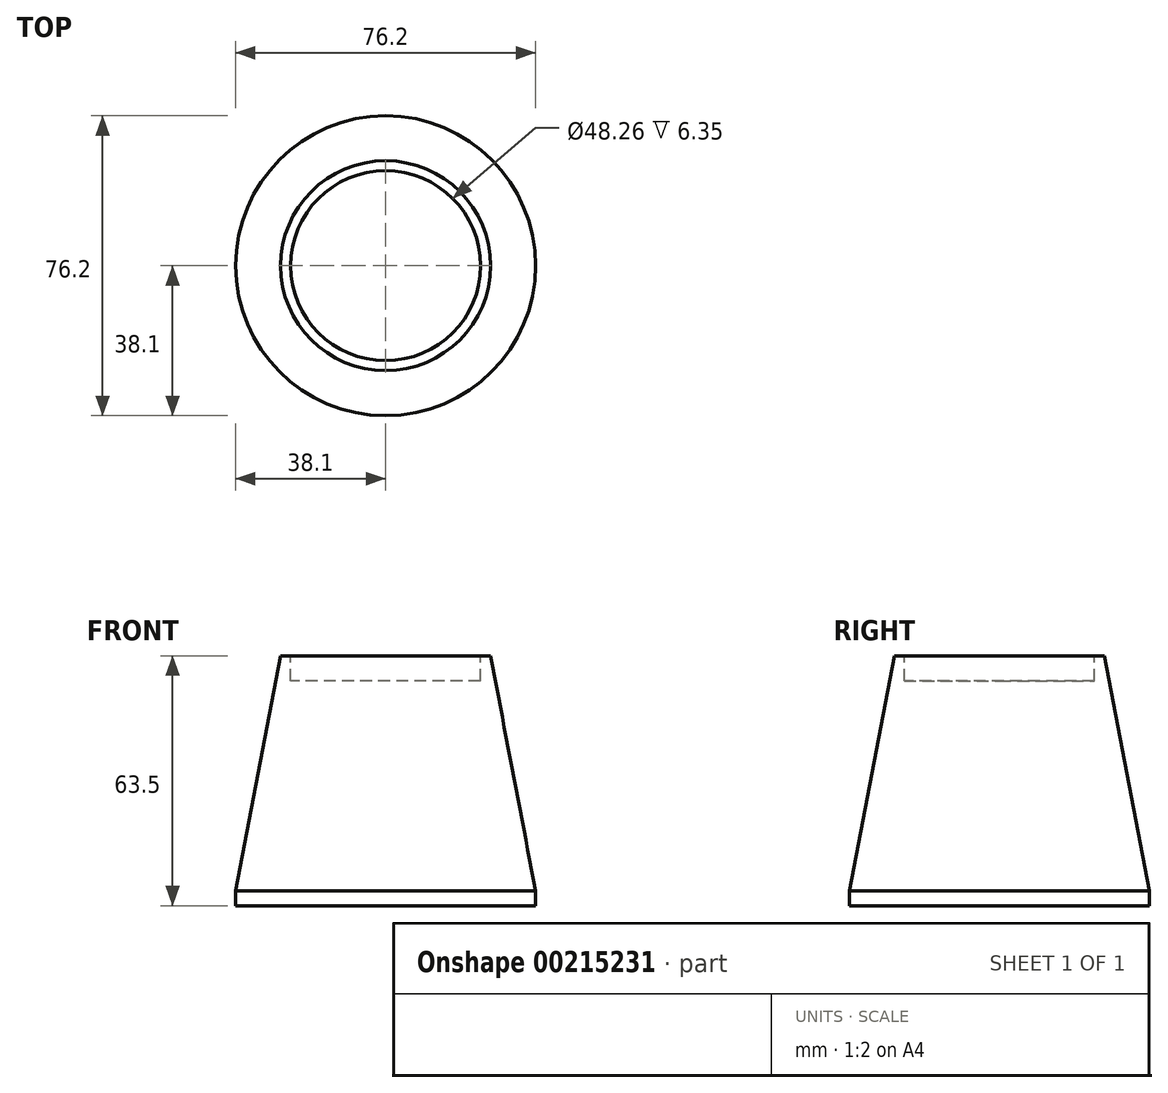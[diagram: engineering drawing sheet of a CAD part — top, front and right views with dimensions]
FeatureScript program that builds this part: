
annotation { "Feature Type Name" : "Feature", "Feature Type Description" : "" }
export const myFeature = defineFeature(function(context is Context, id is Id, definition is map)
    precondition{}
    {
        {
            var Q0;
            Q0=qCreatedBy(makeId("Top.planeOp"),FACE);
            var sketch = newSketch(context, id + "F0", { "sketchPlane" : qUnion([Q0])});
            skCircle(sketch, "E0", {"center": v(0, 0) * mm, "radius": 38.1 * mm});
            skSolve(sketch);
        }
        {
            var Q0;
            Q0=makeQuery(id+"F0.imprint","IMPRINT",FACE,{"disambiguationData":[TD([[makeQuery(id+"F0.imprint","IMPRINT",EDGE,{"derivedFrom":sQuery(id+"F0.wireOp",EDGE,"E0")}),1.0]])]});
            extrude(context, id + "F1", {"entities" : qUnion([Q0]), "depth" : 3.8 * mm});
        }
        {
            var Q0;
            Q0=qCreatedBy(makeId("Top.planeOp"),FACE);
            cPlane(context, id + "F2", {"entities" : qUnion([Q0]), "cplaneType" : CPlaneType.OFFSET, "offset" : 63.5 * mm, "width" : 152.4 * mm, "height" : 152.4 * mm});
        }
        {
            var Q0;
            Q0=qCreatedBy(id+"F2.planeOp",FACE);
            var sketch = newSketch(context, id + "F3", { "sketchPlane" : qUnion([Q0])});
            skCircle(sketch, "E1", {"center": v(0, 0) * mm, "radius": 26.67 * mm});
            skSolve(sketch);
        }
        {
            var Q1;
            Q1=makeQuery(id+"F1.opExtrude","CAP_FACE",FACE,{"disambiguationData":[OSD([sQuery(id+"F0.wireOp",EDGE,"E0")])],"isStart":false});
            var Q2;
            Q2=makeQuery(id+"F3.imprint","IMPRINT",FACE,{"disambiguationData":[TD([[makeQuery(id+"F3.imprint","IMPRINT",EDGE,{"derivedFrom":sQuery(id+"F3.wireOp",EDGE,"E1")}),1.0]])]});
            loft(context, id + "F4", {"operationType" : NewBodyOperationType.ADD, "sheetProfilesArray" : [{ "sheetProfileEntities" : qUnion([Q1]) }, { "sheetProfileEntities" : qUnion([Q2]) }]});
        }
        {
            var Q0;
            Q0=makeQuery(id+"F4.opLoft","CAP_FACE",FACE,{"disambiguationData":[OSD([makeQuery(id+"F3.imprint","IMPRINT",FACE,{"disambiguationData":[TD([[makeQuery(id+"F3.imprint","IMPRINT",EDGE,{"derivedFrom":sQuery(id+"F3.wireOp",EDGE,"E1")}),1.0]])]})])],"isStart":true});
            var sketch = newSketch(context, id + "F5", { "sketchPlane" : qUnion([Q0])});
            skCircle(sketch, "E2", {"center": v(0, 0) * mm, "radius": 24.13 * mm});
            skSolve(sketch);
        }
        {
            var Q0;
            Q0=makeQuery(id+"F5.imprint","IMPRINT",FACE,{"disambiguationData":[TD([[makeQuery(id+"F5.imprint","IMPRINT",EDGE,{"derivedFrom":sQuery(id+"F5.wireOp",EDGE,"E2")}),1.0]])]});
            extrude(context, id + "F6", {"entities" : qUnion([Q0]), "operationType" : NewBodyOperationType.REMOVE, "oppositeDirection" : true, "depth" : 6.35 * mm});
        }
    });
